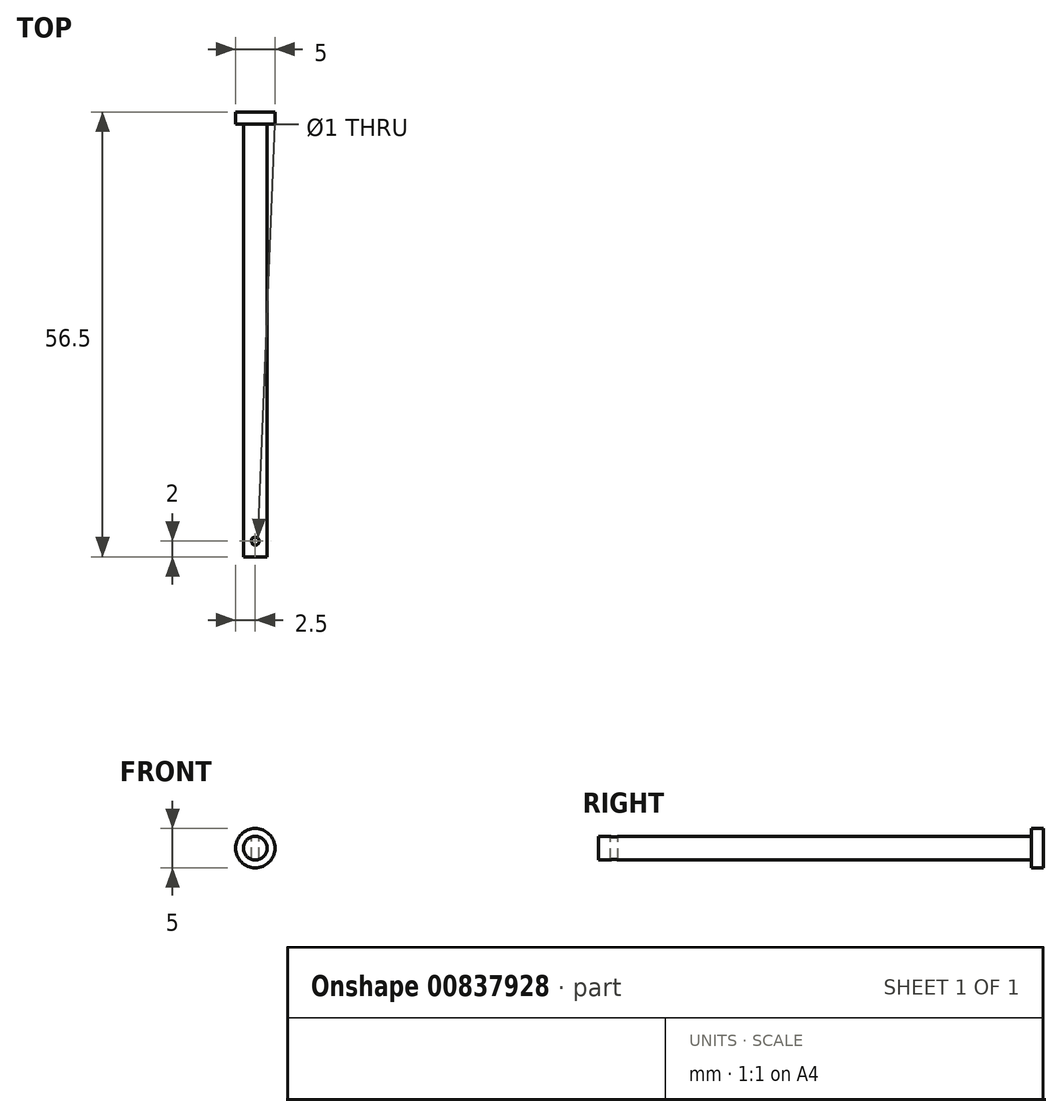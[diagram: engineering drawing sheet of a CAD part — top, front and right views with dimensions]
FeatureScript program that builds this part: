
annotation { "Feature Type Name" : "Feature", "Feature Type Description" : "" }
export const myFeature = defineFeature(function(context is Context, id is Id, definition is map)
    precondition{}
    {
        {
            var Q0;
            Q0=qCreatedBy(makeId("Front.planeOp"),FACE);
            var sketch = newSketch(context, id + "F0", { "sketchPlane" : qUnion([Q0])});
            skCircle(sketch, "E0", {"center": v(0, 0) * mm, "radius": 1.5 * mm});
            skSolve(sketch);
        }
        {
            var Q0;
            Q0=makeQuery(id+"F0.imprint","IMPRINT",FACE,{"disambiguationData":[TD([[makeQuery(id+"F0.imprint","IMPRINT",EDGE,{"derivedFrom":sQuery(id+"F0.wireOp",EDGE,"E0")}),1.0]])]});
            extrude(context, id + "F1", {"entities" : qUnion([Q0]), "depth" : 55 * mm, "offsetDistance" : 25 * mm});
        }
        {
            var Q0;
            Q0=makeQuery(id+"F1.opExtrude","CAP_FACE",FACE,{"disambiguationData":[OSD([sQuery(id+"F0.wireOp",EDGE,"E0")])],"isStart":true});
            var sketch = newSketch(context, id + "F2", { "sketchPlane" : qUnion([Q0])});
            skCircle(sketch, "E1", {"center": v(0, 0) * mm, "radius": 2.5 * mm});
            skSolve(sketch);
        }
        {
            var Q0;
            Q0=makeQuery(id+"F2.imprint","IMPRINT",FACE,{"disambiguationData":[TD([[makeQuery(id+"F2.imprint","IMPRINT",EDGE,{"derivedFrom":sQuery(id+"F2.wireOp",EDGE,"E1")}),1.0]])]});
            var Q1;
            Q1=makeQuery(id+"F2.imprint","IMPRINT",FACE,{"disambiguationData":[TD([[makeQuery(id+"F2.imprint","IMPRINT",EDGE,{"derivedFrom":makeQuery(id+"F1.opExtrude","CAP_EDGE",EDGE,{"disambiguationData":[OSD([sQuery(id+"F0.wireOp",EDGE,"E0")])],"isStart":true})}),-1.0]])]});
            extrude(context, id + "F3", {"entities" : qUnion([Q0, Q1]), "operationType" : NewBodyOperationType.ADD, "depth" : 1.5 * mm, "offsetDistance" : 25 * mm});
        }
        {
            var Q0;
            Q0=qCreatedBy(makeId("Top.planeOp"),FACE);
            var sketch = newSketch(context, id + "F4", { "sketchPlane" : qUnion([Q0])});
            skCircle(sketch, "E2", {"center": v(0, -53) * mm, "radius": 0.5 * mm});
            skSolve(sketch);
        }
        {
            var Q0;
            Q0 = qSketchRegion(id + "F4", true);
            extrude(context, id + "F5", {"entities" : qUnion([Q0]), "operationType" : NewBodyOperationType.REMOVE, "endBound" : BoundingType.SYMMETRIC, "oppositeDirection" : true, "depth" : 5 * mm, "offsetDistance" : 25 * mm});
        }
    });
